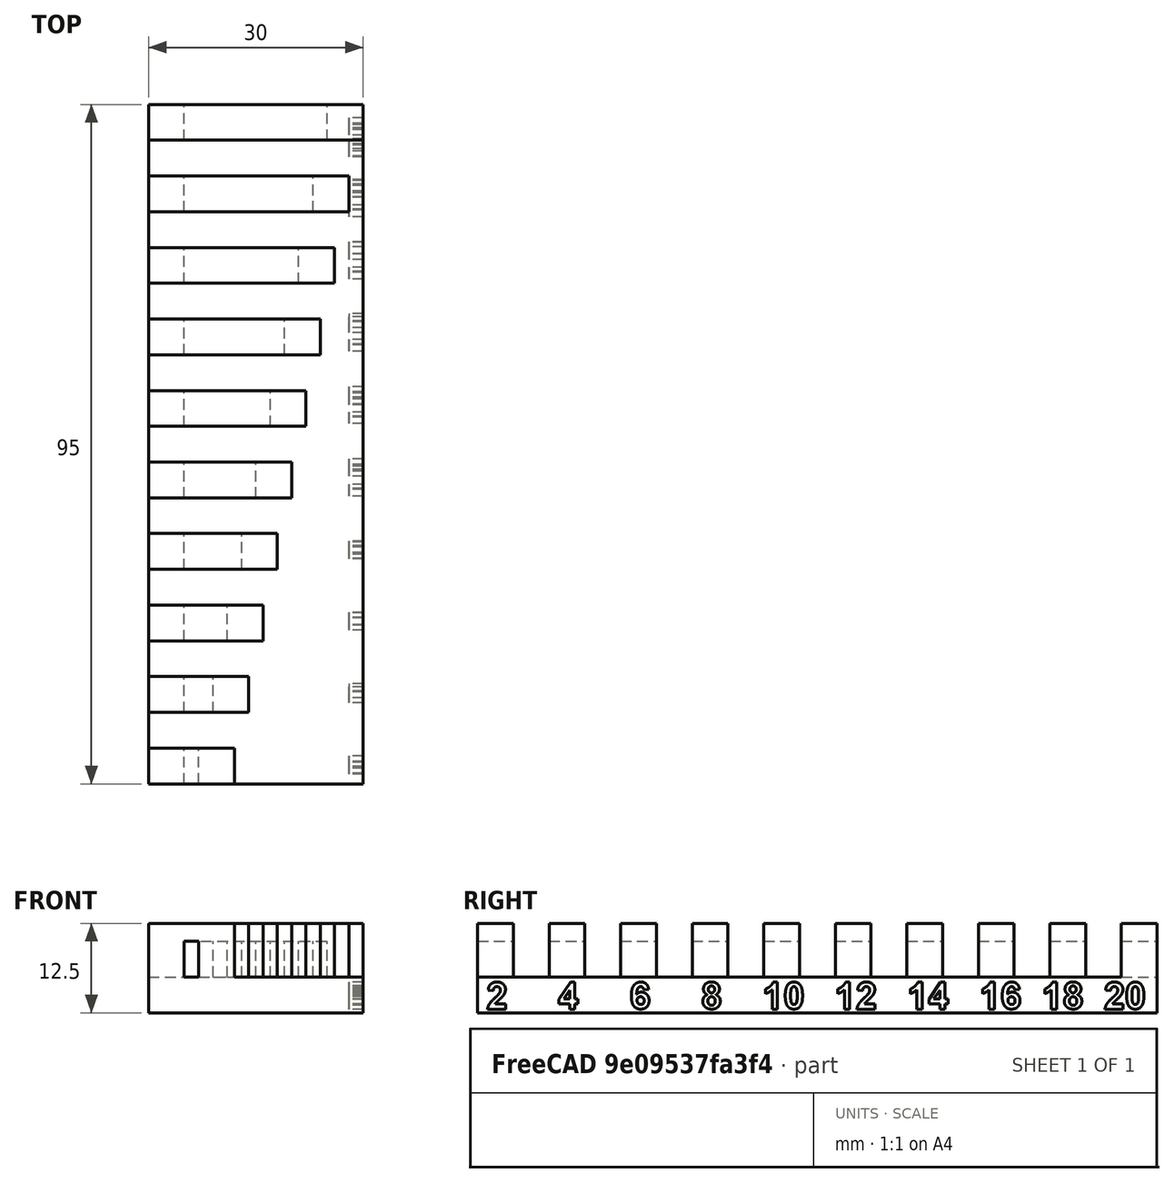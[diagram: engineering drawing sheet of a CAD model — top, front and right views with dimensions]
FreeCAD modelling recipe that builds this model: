
FCSTD DOCUMENT  (FreeCAD 0.18.3R)
Label: ooverhang
License: All rights reserved
LicenseURL: http://en.wikipedia.org/wiki/All_rights_reserved
objects: Part::Box×31, Part::MultiFuse×11, Part::Part2DObjectPython×1, Part::Extrusion×1, Part::Cut×1
note: 45 computed .brp shape members not serialized (recipe doc carries the construction recipe); baked Part::Feature solids carry a one-line shape summary decoded from their .brp

FEATURE [Part::Box] Box  label="Cube"
  AttacherType = Attacher::AttachEngine3D
  Height = 5
  Length = 5
  Width = 5
FEATURE [Part::Box] Box001  label="Cube001"
  AttacherType = Attacher::AttachEngine3D
  Height = 5
  Length = 5
  Placement = pos=(7,0,0) rot=(0,0,1;0rad)
  Width = 5
FEATURE [Part::Box] Box002  label="Cube002"
  AttacherType = Attacher::AttachEngine3D
  Height = 2.5
  Length = 12
  Placement = pos=(0,0,5) rot=(0,0,1;0rad)
  Width = 5
FEATURE [Part::MultiFuse] Fusion  label="2"
  Shapes = -> [Box002,Box,Box001]
FEATURE [Part::Box] Box003  label="Cube003"
  AttacherType = Attacher::AttachEngine3D
  Height = 2.5
  Length = 14
  Placement = pos=(0,10,5) rot=(0,0,1;0rad)
  Width = 5
FEATURE [Part::Box] Box004  label="Cube004"
  AttacherType = Attacher::AttachEngine3D
  Height = 5
  Length = 5
  Placement = pos=(0,10,0) rot=(0,0,1;0rad)
  Width = 5
FEATURE [Part::Box] Box005  label="Cube005"
  AttacherType = Attacher::AttachEngine3D
  Height = 5
  Length = 5
  Placement = pos=(9,10,0) rot=(0,0,1;0rad)
  Width = 5
FEATURE [Part::MultiFuse] Fusion001  label="4"
  Shapes = -> [Box003,Box004,Box005]
FEATURE [Part::Box] Box006  label="Cube006"
  AttacherType = Attacher::AttachEngine3D
  Height = 2.5
  Length = 16
  Placement = pos=(0,20,5) rot=(0,0,1;0rad)
  Width = 5
FEATURE [Part::Box] Box007  label="Cube007"
  AttacherType = Attacher::AttachEngine3D
  Height = 5
  Length = 5
  Placement = pos=(0,20,0) rot=(0,0,1;0rad)
  Width = 5
FEATURE [Part::Box] Box008  label="Cube008"
  AttacherType = Attacher::AttachEngine3D
  Height = 5
  Length = 5
  Placement = pos=(11,20,0) rot=(0,0,1;0rad)
  Width = 5
FEATURE [Part::MultiFuse] Fusion002  label="6"
  Shapes = -> [Box006,Box007,Box008]
FEATURE [Part::Box] Box009  label="base"
  AttacherType = Attacher::AttachEngine3D
  Height = 5
  Length = 30
  Placement = pos=(0,0,-5) rot=(0,0,1;0rad)
  Width = 95
FEATURE [Part::Box] Box010  label="Cube009"
  AttacherType = Attacher::AttachEngine3D
  Height = 2.5
  Length = 18
  Placement = pos=(0,30,5) rot=(0,0,1;0rad)
  Width = 5
FEATURE [Part::Box] Box011  label="Cube010"
  AttacherType = Attacher::AttachEngine3D
  Height = 5
  Length = 5
  Placement = pos=(13,30,0) rot=(0,0,1;0rad)
  Width = 5
FEATURE [Part::Box] Box012  label="Cube011"
  AttacherType = Attacher::AttachEngine3D
  Height = 5
  Length = 5
  Placement = pos=(0,30,0) rot=(0,0,1;0rad)
  Width = 5
FEATURE [Part::MultiFuse] Fusion004  label="8"
  Shapes = -> [Box010,Box012,Box011]
FEATURE [Part::Box] Box013  label="Cube012"
  AttacherType = Attacher::AttachEngine3D
  Height = 5
  Length = 5
  Placement = pos=(0,40,0) rot=(0,0,1;0rad)
  Width = 5
FEATURE [Part::Box] Box014  label="Cube013"
  AttacherType = Attacher::AttachEngine3D
  Height = 5
  Length = 5
  Placement = pos=(15,40,0) rot=(0,0,1;0rad)
  Width = 5
FEATURE [Part::Box] Box015  label="Cube014"
  AttacherType = Attacher::AttachEngine3D
  Height = 2.5
  Length = 20
  Placement = pos=(0,40,5) rot=(0,0,1;0rad)
  Width = 5
FEATURE [Part::MultiFuse] Fusion005  label="10"
  Shapes = -> [Box015,Box013,Box014]
FEATURE [Part::Box] Box016  label="Cube015"
  AttacherType = Attacher::AttachEngine3D
  Height = 5
  Length = 5
  Placement = pos=(17,50,0) rot=(0,0,1;0rad)
  Width = 5
FEATURE [Part::Box] Box017  label="Cube016"
  AttacherType = Attacher::AttachEngine3D
  Height = 5
  Length = 5
  Placement = pos=(0,50,0) rot=(0,0,1;0rad)
  Width = 5
FEATURE [Part::Box] Box018  label="Cube017"
  AttacherType = Attacher::AttachEngine3D
  Height = 2.5
  Length = 22
  Placement = pos=(0,50,5) rot=(0,0,1;0rad)
  Width = 5
FEATURE [Part::MultiFuse] Fusion006  label="12"
  Shapes = -> [Box018,Box017,Box016]
FEATURE [Part::Box] Box019  label="Cube018"
  AttacherType = Attacher::AttachEngine3D
  Height = 5
  Length = 5
  Placement = pos=(19,60,0) rot=(0,0,1;0rad)
  Width = 5
FEATURE [Part::Box] Box020  label="Cube019"
  AttacherType = Attacher::AttachEngine3D
  Height = 5
  Length = 5
  Placement = pos=(0,60,0) rot=(0,0,1;0rad)
  Width = 5
FEATURE [Part::Box] Box021  label="Cube020"
  AttacherType = Attacher::AttachEngine3D
  Height = 2.5
  Length = 24
  Placement = pos=(0,60,5) rot=(0,0,1;0rad)
  Width = 5
FEATURE [Part::MultiFuse] Fusion007  label="14"
  Shapes = -> [Box021,Box020,Box019]
FEATURE [Part::Box] Box022  label="Cube021"
  AttacherType = Attacher::AttachEngine3D
  Height = 5
  Length = 5
  Placement = pos=(21,70,0) rot=(0,0,1;0rad)
  Width = 5
FEATURE [Part::Box] Box023  label="Cube022"
  AttacherType = Attacher::AttachEngine3D
  Height = 2.5
  Length = 26
  Placement = pos=(0,70,5) rot=(0,0,1;0rad)
  Width = 5
FEATURE [Part::Box] Box024  label="Cube023"
  AttacherType = Attacher::AttachEngine3D
  Height = 5
  Length = 5
  Placement = pos=(0,70,0) rot=(0,0,1;0rad)
  Width = 5
FEATURE [Part::MultiFuse] Fusion008  label="16"
  Shapes = -> [Box023,Box024,Box022]
FEATURE [Part::Box] Box025  label="Cube024"
  AttacherType = Attacher::AttachEngine3D
  Height = 5
  Length = 5
  Placement = pos=(23,80,0) rot=(0,0,1;0rad)
  Width = 5
FEATURE [Part::Box] Box026  label="Cube025"
  AttacherType = Attacher::AttachEngine3D
  Height = 2.5
  Length = 28
  Placement = pos=(0,80,5) rot=(0,0,1;0rad)
  Width = 5
FEATURE [Part::Box] Box027  label="Cube026"
  AttacherType = Attacher::AttachEngine3D
  Height = 5
  Length = 5
  Placement = pos=(0,80,0) rot=(0,0,1;0rad)
  Width = 5
FEATURE [Part::MultiFuse] Fusion009  label="18"
  Shapes = -> [Box026,Box027,Box025]
FEATURE [Part::Box] Box028  label="Cube027"
  AttacherType = Attacher::AttachEngine3D
  Height = 2.5
  Length = 30
  Placement = pos=(0,90,5) rot=(0,0,1;0rad)
  Width = 5
FEATURE [Part::Box] Box029  label="Cube028"
  AttacherType = Attacher::AttachEngine3D
  Height = 5
  Length = 5
  Placement = pos=(25,90,0) rot=(0,0,1;0rad)
  Width = 5
FEATURE [Part::Box] Box030  label="Cube029"
  AttacherType = Attacher::AttachEngine3D
  Height = 5
  Length = 5
  Placement = pos=(0,90,0) rot=(0,0,1;0rad)
  Width = 5
FEATURE [Part::MultiFuse] Fusion010  label="20"
  Shapes = -> [Box028,Box030,Box029]
FEATURE [Part::MultiFuse] Fusion003  label="overhangs"
  Shapes = -> [Box009,Fusion002,Fusion001,Fusion,Fusion004,Fusion005,Fusion006,Fusion007,Fusion008,Fusion009,Fusion010]
FEATURE [Part::Part2DObjectPython] ShapeString  # Draft 2D object (typed FeaturePython)
  FontFile = <userpath>/git/aws2/bin/fonts/Arial Bold.ttf
  Placement = pos=(30,1.26,-4.5) rot=(0.57735,0.57735,0.57735;2.0944rad)
  Size = 4
  String = 2     4     6     8    10   12   14   16  18  20
  Support = -> [Fusion003]
  Tracking = 0
FEATURE [Part::Extrusion] Extrude
  Base = -> ShapeString
  Dir = (1,-1e-16,2e-16)
  DirMode = 2
  FaceMakerClass = Part::FaceMakerBullseye
  LengthFwd = -2
  LengthRev = 0
  Solid = false
  Symmetric = false
FEATURE [Part::Cut] Cut
  Base = -> Fusion003
  Tool = -> Extrude
